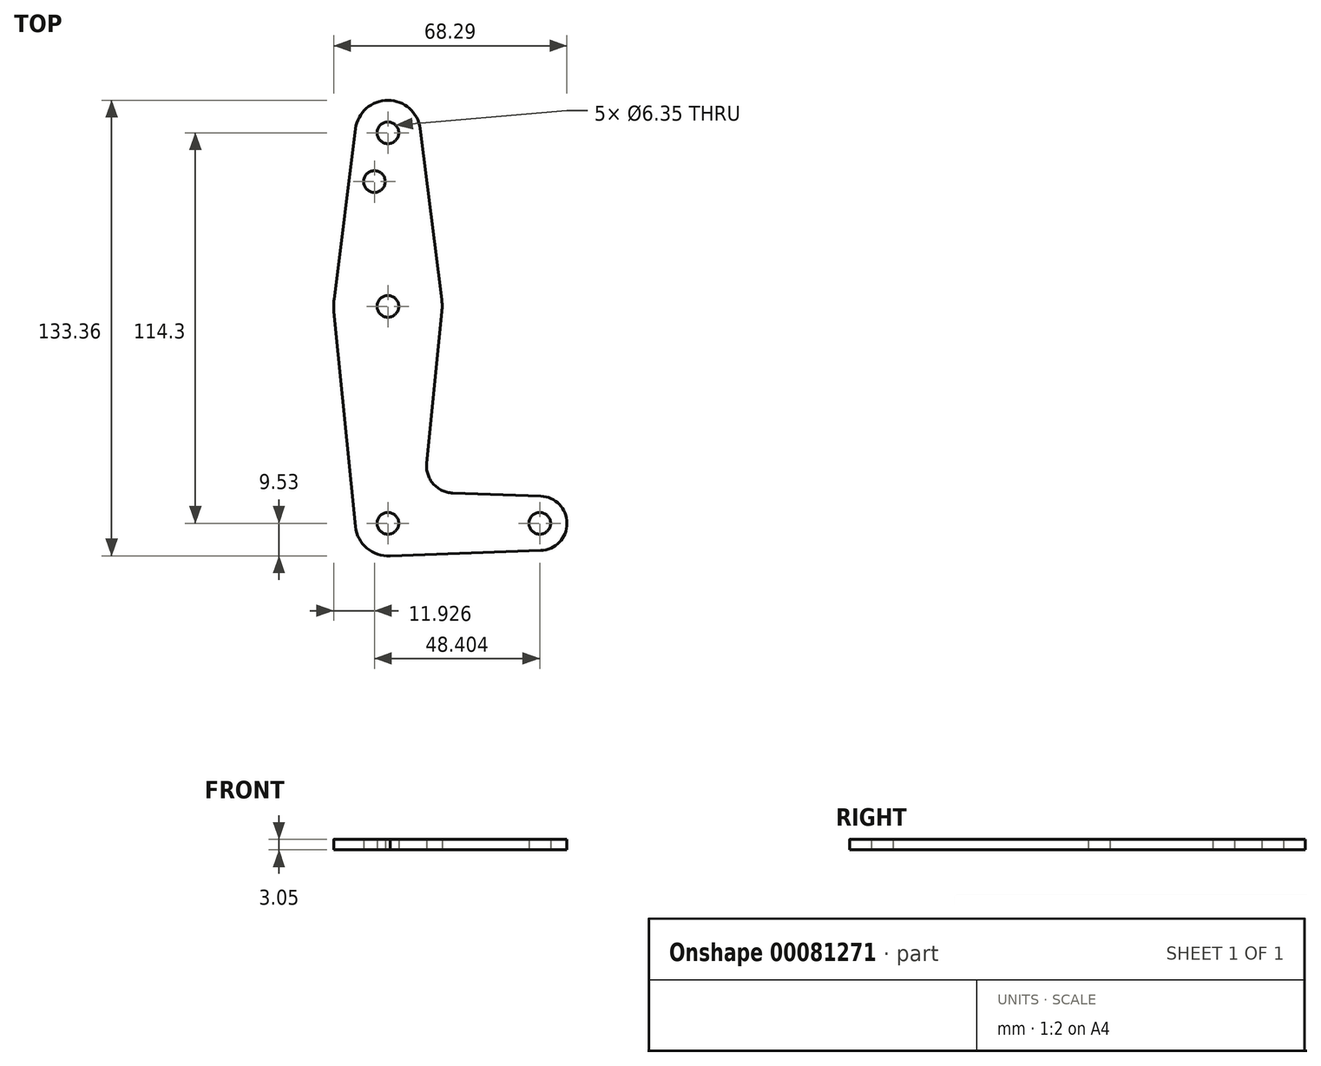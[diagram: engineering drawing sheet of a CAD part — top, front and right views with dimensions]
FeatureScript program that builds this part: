
annotation { "Feature Type Name" : "Feature", "Feature Type Description" : "" }
export const myFeature = defineFeature(function(context is Context, id is Id, definition is map)
    precondition{}
    {
        {
            var Q0;
            Q0=qCreatedBy(makeId("Top.planeOp"),FACE);
            var sketch = newSketch(context, id + "F0", { "sketchPlane" : qUnion([Q0])});
            skLineSegment(sketch, "E0", {"start": v(0, 0) * mm, "end": v(0, 114.3) * mm, "construction": true});
            skCircle(sketch, "E1", {"center": v(0, 0) * mm, "radius": 9.53 * mm});
            skCircle(sketch, "E2", {"center": v(0, 114.3) * mm, "radius": 9.53 * mm});
            skLineSegment(sketch, "E3", {"start": v(0, 0) * mm, "end": v(44.45, 0) * mm, "construction": true});
            skCircle(sketch, "E4", {"center": v(44.45, 0) * mm, "radius": 7.96 * mm});
            skCircle(sketch, "E5", {"center": v(0, 63.5) * mm, "radius": 15.88 * mm});
            skLineSegment(sketch, "E6", {"start": v(9.45, 115.5) * mm, "end": v(15.75, 65.48) * mm});
            skLineSegment(sketch, "E7", {"start": v(-9.45, 115.5) * mm, "end": v(-15.75, 65.48) * mm});
            skLineSegment(sketch, "E8", {"start": v(-15.8, 61.91) * mm, "end": v(-9.48, -0.95) * mm});
            skLineSegment(sketch, "E9", {"start": v(15.8, 61.91) * mm, "end": v(11.34, 17.6) * mm});
            skLineSegment(sketch, "E10", {"start": v(18.97, 8.86) * mm, "end": v(44.73, 7.96) * mm});
            skLineSegment(sketch, "E11", {"start": v(0, -9.53) * mm, "end": v(44.73, -7.96) * mm});
            skCircle(sketch, "E12", {"center": v(0, 114.3) * mm, "radius": 3.18 * mm});
            skCircle(sketch, "E13", {"center": v(0, 63.5) * mm, "radius": 3.18 * mm});
            skCircle(sketch, "E14", {"center": v(0, 0) * mm, "radius": 3.18 * mm});
            skCircle(sketch, "E15", {"center": v(-3.95, 100.03) * mm, "radius": 3.18 * mm});
            skCircle(sketch, "E16", {"center": v(44.45, 0) * mm, "radius": 3.18 * mm});
            skArc(sketch, "E17.filletArc", {"start": v(11.34, 17.6) * mm, "mid": v(13.26, 11.58) * mm, "end": v(18.97, 8.86) * mm});
            skSolve(sketch);
        }
        {
            var Q0;
            Q0 = qSketchRegion(id + "F0", true);
            extrude(context, id + "F1", {"entities" : qUnion([Q0]), "depth" : 3.05 * mm});
        }
    });
